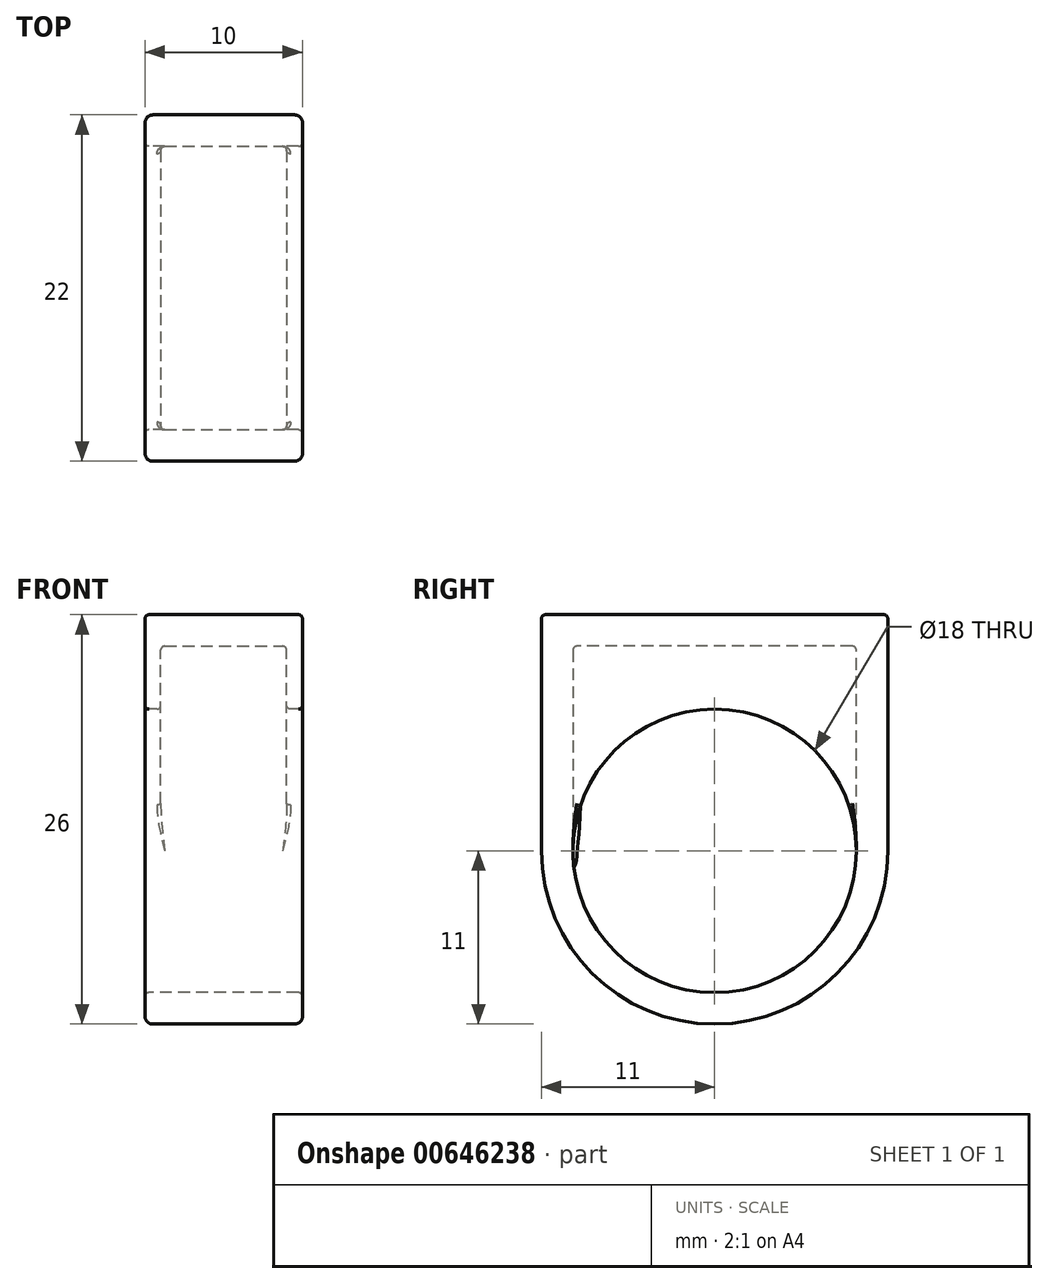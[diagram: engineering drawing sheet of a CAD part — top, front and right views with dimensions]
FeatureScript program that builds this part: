
annotation { "Feature Type Name" : "Feature", "Feature Type Description" : "" }
export const myFeature = defineFeature(function(context is Context, id is Id, definition is map)
    precondition{}
    {
        {
            var Q0;
            Q0=qCreatedBy(makeId("Right.planeOp"),FACE);
            var sketch = newSketch(context, id + "F0", { "sketchPlane" : qUnion([Q0])});
            skCircle(sketch, "E0", {"center": v(0, 0) * mm, "radius": 9 * mm});
            skArc(sketch, "E1", {"start": v(-11, 0) * mm, "mid": v(0, -11) * mm, "end": v(11, 0) * mm});
            skLineSegment(sketch, "E2", {"start": v(11, 0) * mm, "end": v(11, 15) * mm});
            skLineSegment(sketch, "E3", {"start": v(11, 15) * mm, "end": v(-11, 15) * mm});
            skLineSegment(sketch, "E4", {"start": v(-11, 0) * mm, "end": v(-11, 15) * mm});
            skSolve(sketch);
        }
        {
            var Q0;
            Q0 = qSketchRegion(id + "F0", true);
            extrude(context, id + "F1", {"entities" : qUnion([Q0]), "endBound" : BoundingType.SYMMETRIC, "depth" : 10 * mm, "offsetDistance" : 25 * mm});
        }
        {
            var Q0;
            Q0=qCreatedBy(makeId("Right.planeOp"),FACE);
            var sketch = newSketch(context, id + "F2", { "sketchPlane" : qUnion([Q0])});
            skLineSegment(sketch, "E5.0", {"start": v(-9, 13) * mm, "end": v(-9, 0) * mm});
            skLineSegment(sketch, "E5.1", {"start": v(9, 13) * mm, "end": v(-9, 13) * mm});
            skLineSegment(sketch, "E5.2", {"start": v(9, 0) * mm, "end": v(9, 13) * mm});
            skArc(sketch, "E5.3", {"start": v(-9, 0) * mm, "mid": v(0, -9) * mm, "end": v(9, 0) * mm});
            skSolve(sketch);
        }
        {
            var Q0;
            Q0 = qSketchRegion(id + "F2", true);
            extrude(context, id + "F3", {"entities" : qUnion([Q0]), "operationType" : NewBodyOperationType.REMOVE, "endBound" : BoundingType.SYMMETRIC, "oppositeDirection" : true, "depth" : 8 * mm, "offsetDistance" : 25 * mm});
        }
        {
            var Q0;
            Q0=makeQuery(id+"F1.opExtrude","CAP_EDGE",EDGE,{"disambiguationData":[OSD([sQuery(id+"F0.wireOp",EDGE,"E2")])],"isStart":false});
            var Q1;
            Q1=makeQuery(id+"F1.opExtrude","CAP_EDGE",EDGE,{"disambiguationData":[OSD([sQuery(id+"F0.wireOp",EDGE,"E2")])],"isStart":true});
            fillet(context, id + "F4", {"entities" : qUnion([Q0, Q1]), "radius" : .5 * mm, "tangentPropagation" : true, "allowEdgeOverflow" : false});
        }
        {
            var Q0;
            Q0=makeQuery(id+"F4.opFillet","BLEND_EDGE",EDGE,{"blendedFrom":[makeQuery(id+"F1.opExtrude","CAP_EDGE",EDGE,{"disambiguationData":[OSD([sQuery(id+"F0.wireOp",EDGE,"E2")])],"isStart":true}),makeQuery(id+"F1.opExtrude","SWEPT_FACE",FACE,{"disambiguationData":[OSD([sQuery(id+"F0.wireOp",EDGE,"E3")])]})],"blendedInto":[makeQuery(id+"F1.opExtrude","SWEPT_FACE",FACE,{"disambiguationData":[OSD([sQuery(id+"F0.wireOp",EDGE,"E3")])]})]});
            var Q1;
            Q1=makeQuery(id+"F3.boolean.opBoolean","INTERSECT",EDGE,{"derivedFrom":[makeQuery(id+"F1.opExtrude","SWEPT_FACE",FACE,{"disambiguationData":[OSD([sQuery(id+"F0.wireOp",EDGE,"E0")])]}),makeQuery(id+"F3.opExtrude","CAP_FACE",FACE,{"disambiguationData":[OSD([sQuery(id+"F2.wireOp",EDGE,"E5.0"),sQuery(id+"F2.wireOp",EDGE,"E5.1"),sQuery(id+"F2.wireOp",EDGE,"E5.2"),sQuery(id+"F2.wireOp",EDGE,"E5.3")])],"isStart":false})]});
            var Q2;
            Q2=makeQuery(id+"F1.opExtrude","CAP_EDGE",EDGE,{"disambiguationData":[OSD([sQuery(id+"F0.wireOp",EDGE,"E0")])],"isStart":true});
            var Q3;
            Q3=makeQuery(id+"F4.opFillet","BLEND_EDGE",EDGE,{"blendedFrom":[makeQuery(id+"F1.opExtrude","CAP_EDGE",EDGE,{"disambiguationData":[OSD([sQuery(id+"F0.wireOp",EDGE,"E1")])],"isStart":true}),makeQuery(id+"F1.opExtrude","CAP_EDGE",EDGE,{"disambiguationData":[OSD([sQuery(id+"F0.wireOp",EDGE,"E2")])],"isStart":true})],"blendedInto":[]});
            var Q4;
            {var subQ0=sQuery(id+"F0.wireOp",EDGE,"E1");Q4=makeQuery(id+"F4.opFillet","BLEND_EDGE",EDGE,{"blendedFrom":[makeQuery(id+"F1.opExtrude","CAP_EDGE",EDGE,{"disambiguationData":[OSD([subQ0])],"isStart":true}),makeQuery(id+"F1.opExtrude","CAP_FACE",FACE,{"disambiguationData":[OSD([sQuery(id+"F0.wireOp",EDGE,"E0"),subQ0,sQuery(id+"F0.wireOp",EDGE,"E2"),sQuery(id+"F0.wireOp",EDGE,"E3"),sQuery(id+"F0.wireOp",EDGE,"E4")])],"isStart":true})],"blendedInto":[makeQuery(id+"F1.opExtrude","CAP_FACE",FACE,{"disambiguationData":[OSD([sQuery(id+"F0.wireOp",EDGE,"E0"),subQ0,sQuery(id+"F0.wireOp",EDGE,"E2"),sQuery(id+"F0.wireOp",EDGE,"E3"),sQuery(id+"F0.wireOp",EDGE,"E4")])],"isStart":true})]});}
            var Q5;
            Q5=makeQuery(id+"F3.boolean.opBoolean","COPY",EDGE,{"derivedFrom":makeQuery(id+"F3.opExtrude","SWEPT_EDGE",EDGE,{"disambiguationData":[OSD([sQuery(id+"F2.wireOp",EDGE,"E5.0"),sQuery(id+"F2.wireOp",EDGE,"E5.3")])]})});
            var Q6;
            {var subQ0=sQuery(id+"F0.wireOp",EDGE,"E1");Q6=makeQuery(id+"F4.opFillet","BLEND_EDGE",EDGE,{"blendedFrom":[makeQuery(id+"F1.opExtrude","CAP_EDGE",EDGE,{"disambiguationData":[OSD([subQ0])],"isStart":true}),makeQuery(id+"F1.opExtrude","SWEPT_FACE",FACE,{"disambiguationData":[OSD([subQ0])]})],"blendedInto":[makeQuery(id+"F1.opExtrude","SWEPT_FACE",FACE,{"disambiguationData":[OSD([subQ0])]})]});}
            var Q7;
            {var subQ0=sQuery(id+"F0.wireOp",EDGE,"E1");Q7=makeQuery(id+"F4.opFillet","BLEND_EDGE",EDGE,{"blendedFrom":[makeQuery(id+"F1.opExtrude","CAP_EDGE",EDGE,{"disambiguationData":[OSD([subQ0])],"isStart":false}),makeQuery(id+"F1.opExtrude","SWEPT_FACE",FACE,{"disambiguationData":[OSD([subQ0])]})],"blendedInto":[makeQuery(id+"F1.opExtrude","SWEPT_FACE",FACE,{"disambiguationData":[OSD([subQ0])]})]});}
            var Q8;
            Q8=makeQuery(id+"F1.opExtrude","CAP_EDGE",EDGE,{"disambiguationData":[OSD([sQuery(id+"F0.wireOp",EDGE,"E3")])],"isStart":true});
            var Q9;
            Q9=makeQuery(id+"F1.opExtrude","CAP_EDGE",EDGE,{"disambiguationData":[OSD([sQuery(id+"F0.wireOp",EDGE,"E3")])],"isStart":false});
            var Q10;
            {var subQ0=sQuery(id+"F0.wireOp",EDGE,"E2");Q10=makeQuery(id+"F4.opFillet","BLEND_EDGE",EDGE,{"blendedFrom":[makeQuery(id+"F1.opExtrude","CAP_EDGE",EDGE,{"disambiguationData":[OSD([subQ0])],"isStart":true}),makeQuery(id+"F1.opExtrude","SWEPT_FACE",FACE,{"disambiguationData":[OSD([subQ0])]})],"blendedInto":[makeQuery(id+"F1.opExtrude","SWEPT_FACE",FACE,{"disambiguationData":[OSD([subQ0])]})]});}
            var Q11;
            {var subQ0=sQuery(id+"F0.wireOp",EDGE,"E2");Q11=makeQuery(id+"F4.opFillet","BLEND_EDGE",EDGE,{"blendedFrom":[makeQuery(id+"F1.opExtrude","CAP_EDGE",EDGE,{"disambiguationData":[OSD([subQ0])],"isStart":false}),makeQuery(id+"F1.opExtrude","CAP_FACE",FACE,{"disambiguationData":[OSD([sQuery(id+"F0.wireOp",EDGE,"E0"),sQuery(id+"F0.wireOp",EDGE,"E1"),subQ0,sQuery(id+"F0.wireOp",EDGE,"E3"),sQuery(id+"F0.wireOp",EDGE,"E4")])],"isStart":false})],"blendedInto":[makeQuery(id+"F1.opExtrude","CAP_FACE",FACE,{"disambiguationData":[OSD([sQuery(id+"F0.wireOp",EDGE,"E0"),sQuery(id+"F0.wireOp",EDGE,"E1"),subQ0,sQuery(id+"F0.wireOp",EDGE,"E3"),sQuery(id+"F0.wireOp",EDGE,"E4")])],"isStart":false})]});}
            var Q12;
            Q12=makeQuery(id+"F1.opExtrude","SWEPT_EDGE",EDGE,{"disambiguationData":[OSD([sQuery(id+"F0.wireOp",EDGE,"E1"),sQuery(id+"F0.wireOp",EDGE,"E4")])]});
            var Q13;
            Q13=makeQuery(id+"F1.opExtrude","SWEPT_EDGE",EDGE,{"disambiguationData":[OSD([sQuery(id+"F0.wireOp",EDGE,"E1"),sQuery(id+"F0.wireOp",EDGE,"E2")])]});
            var Q14;
            Q14=makeQuery(id+"F1.opExtrude","SWEPT_EDGE",EDGE,{"disambiguationData":[OSD([sQuery(id+"F0.wireOp",EDGE,"E2"),sQuery(id+"F0.wireOp",EDGE,"E3")])]});
            var Q15;
            Q15=makeQuery(id+"F1.opExtrude","SWEPT_EDGE",EDGE,{"disambiguationData":[OSD([sQuery(id+"F0.wireOp",EDGE,"E3"),sQuery(id+"F0.wireOp",EDGE,"E4")])]});
            var Q16;
            Q16=makeQuery(id+"F4.opFillet","BLEND_EDGE",EDGE,{"blendedFrom":[makeQuery(id+"F1.opExtrude","CAP_EDGE",EDGE,{"disambiguationData":[OSD([sQuery(id+"F0.wireOp",EDGE,"E1")])],"isStart":true}),makeQuery(id+"F1.opExtrude","CAP_EDGE",EDGE,{"disambiguationData":[OSD([sQuery(id+"F0.wireOp",EDGE,"E4")])],"isStart":true})],"blendedInto":[]});
            var Q17;
            Q17=makeQuery(id+"F3.boolean.opBoolean","COPY",EDGE,{"derivedFrom":makeQuery(id+"F3.opExtrude","SWEPT_EDGE",EDGE,{"disambiguationData":[OSD([sQuery(id+"F2.wireOp",EDGE,"E5.2"),sQuery(id+"F2.wireOp",EDGE,"E5.3")])]})});
            var Q18;
            Q18=makeQuery(id+"F3.boolean.opBoolean","COPY",EDGE,{"derivedFrom":makeQuery(id+"F3.opExtrude","CAP_EDGE",EDGE,{"disambiguationData":[OSD([sQuery(id+"F2.wireOp",EDGE,"E5.0")])],"isStart":false})});
            var Q19;
            Q19=makeQuery(id+"F1.opExtrude","CAP_EDGE",EDGE,{"disambiguationData":[OSD([sQuery(id+"F0.wireOp",EDGE,"E0")])],"isStart":false});
            var Q20;
            Q20=makeQuery(id+"F3.boolean.opBoolean","COPY",EDGE,{"derivedFrom":makeQuery(id+"F3.opExtrude","SWEPT_EDGE",EDGE,{"disambiguationData":[OSD([sQuery(id+"F2.wireOp",EDGE,"E5.1"),sQuery(id+"F2.wireOp",EDGE,"E5.2")])]})});
            var Q21;
            Q21=makeQuery(id+"F3.boolean.opBoolean","COPY",EDGE,{"derivedFrom":makeQuery(id+"F3.opExtrude","CAP_EDGE",EDGE,{"disambiguationData":[OSD([sQuery(id+"F2.wireOp",EDGE,"E5.1")])],"isStart":true})});
            var Q22;
            Q22=makeQuery(id+"F3.boolean.opBoolean","COPY",EDGE,{"derivedFrom":makeQuery(id+"F3.opExtrude","CAP_EDGE",EDGE,{"disambiguationData":[OSD([sQuery(id+"F2.wireOp",EDGE,"E5.1")])],"isStart":false})});
            var Q23;
            Q23=makeQuery(id+"F3.boolean.opBoolean","COPY",EDGE,{"derivedFrom":makeQuery(id+"F3.opExtrude","SWEPT_EDGE",EDGE,{"disambiguationData":[OSD([sQuery(id+"F2.wireOp",EDGE,"E5.0"),sQuery(id+"F2.wireOp",EDGE,"E5.1")])]})});
            var Q24;
            Q24=makeQuery(id+"F4.opFillet","BLEND_EDGE",EDGE,{"blendedFrom":[makeQuery(id+"F1.opExtrude","CAP_EDGE",EDGE,{"disambiguationData":[OSD([sQuery(id+"F0.wireOp",EDGE,"E1")])],"isStart":false}),makeQuery(id+"F1.opExtrude","CAP_EDGE",EDGE,{"disambiguationData":[OSD([sQuery(id+"F0.wireOp",EDGE,"E2")])],"isStart":false})],"blendedInto":[]});
            var Q25;
            {var subQ0=sQuery(id+"F0.wireOp",EDGE,"E1");Q25=makeQuery(id+"F4.opFillet","BLEND_EDGE",EDGE,{"blendedFrom":[makeQuery(id+"F1.opExtrude","CAP_EDGE",EDGE,{"disambiguationData":[OSD([subQ0])],"isStart":false}),makeQuery(id+"F1.opExtrude","CAP_FACE",FACE,{"disambiguationData":[OSD([sQuery(id+"F0.wireOp",EDGE,"E0"),subQ0,sQuery(id+"F0.wireOp",EDGE,"E2"),sQuery(id+"F0.wireOp",EDGE,"E3"),sQuery(id+"F0.wireOp",EDGE,"E4")])],"isStart":false})],"blendedInto":[makeQuery(id+"F1.opExtrude","CAP_FACE",FACE,{"disambiguationData":[OSD([sQuery(id+"F0.wireOp",EDGE,"E0"),subQ0,sQuery(id+"F0.wireOp",EDGE,"E2"),sQuery(id+"F0.wireOp",EDGE,"E3"),sQuery(id+"F0.wireOp",EDGE,"E4")])],"isStart":false})]});}
            var Q26;
            {var subQ0=sQuery(id+"F0.wireOp",EDGE,"E2");Q26=makeQuery(id+"F4.opFillet","BLEND_EDGE",EDGE,{"blendedFrom":[makeQuery(id+"F1.opExtrude","CAP_EDGE",EDGE,{"disambiguationData":[OSD([subQ0])],"isStart":true}),makeQuery(id+"F1.opExtrude","CAP_FACE",FACE,{"disambiguationData":[OSD([sQuery(id+"F0.wireOp",EDGE,"E0"),sQuery(id+"F0.wireOp",EDGE,"E1"),subQ0,sQuery(id+"F0.wireOp",EDGE,"E3"),sQuery(id+"F0.wireOp",EDGE,"E4")])],"isStart":true})],"blendedInto":[makeQuery(id+"F1.opExtrude","CAP_FACE",FACE,{"disambiguationData":[OSD([sQuery(id+"F0.wireOp",EDGE,"E0"),sQuery(id+"F0.wireOp",EDGE,"E1"),subQ0,sQuery(id+"F0.wireOp",EDGE,"E3"),sQuery(id+"F0.wireOp",EDGE,"E4")])],"isStart":true})]});}
            var Q27;
            {var subQ0=sQuery(id+"F0.wireOp",EDGE,"E2");Q27=makeQuery(id+"F4.opFillet","BLEND_EDGE",EDGE,{"blendedFrom":[makeQuery(id+"F1.opExtrude","CAP_EDGE",EDGE,{"disambiguationData":[OSD([subQ0])],"isStart":false}),makeQuery(id+"F1.opExtrude","SWEPT_FACE",FACE,{"disambiguationData":[OSD([subQ0])]})],"blendedInto":[makeQuery(id+"F1.opExtrude","SWEPT_FACE",FACE,{"disambiguationData":[OSD([subQ0])]})]});}
            var Q28;
            Q28=makeQuery(id+"F4.opFillet","BLEND_EDGE",EDGE,{"blendedFrom":[makeQuery(id+"F1.opExtrude","CAP_EDGE",EDGE,{"disambiguationData":[OSD([sQuery(id+"F0.wireOp",EDGE,"E2")])],"isStart":false}),makeQuery(id+"F1.opExtrude","SWEPT_FACE",FACE,{"disambiguationData":[OSD([sQuery(id+"F0.wireOp",EDGE,"E3")])]})],"blendedInto":[makeQuery(id+"F1.opExtrude","SWEPT_FACE",FACE,{"disambiguationData":[OSD([sQuery(id+"F0.wireOp",EDGE,"E3")])]})]});
            var Q29;
            {var subQ0=sQuery(id+"F0.wireOp",EDGE,"E4");Q29=makeQuery(id+"F4.opFillet","BLEND_EDGE",EDGE,{"blendedFrom":[makeQuery(id+"F1.opExtrude","CAP_EDGE",EDGE,{"disambiguationData":[OSD([subQ0])],"isStart":true}),makeQuery(id+"F1.opExtrude","CAP_FACE",FACE,{"disambiguationData":[OSD([sQuery(id+"F0.wireOp",EDGE,"E0"),sQuery(id+"F0.wireOp",EDGE,"E1"),sQuery(id+"F0.wireOp",EDGE,"E2"),sQuery(id+"F0.wireOp",EDGE,"E3"),subQ0])],"isStart":true})],"blendedInto":[makeQuery(id+"F1.opExtrude","CAP_FACE",FACE,{"disambiguationData":[OSD([sQuery(id+"F0.wireOp",EDGE,"E0"),sQuery(id+"F0.wireOp",EDGE,"E1"),sQuery(id+"F0.wireOp",EDGE,"E2"),sQuery(id+"F0.wireOp",EDGE,"E3"),subQ0])],"isStart":true})]});}
            var Q30;
            Q30=makeQuery(id+"F4.opFillet","BLEND_EDGE",EDGE,{"blendedFrom":[makeQuery(id+"F1.opExtrude","CAP_EDGE",EDGE,{"disambiguationData":[OSD([sQuery(id+"F0.wireOp",EDGE,"E4")])],"isStart":true}),makeQuery(id+"F1.opExtrude","SWEPT_FACE",FACE,{"disambiguationData":[OSD([sQuery(id+"F0.wireOp",EDGE,"E3")])]})],"blendedInto":[makeQuery(id+"F1.opExtrude","SWEPT_FACE",FACE,{"disambiguationData":[OSD([sQuery(id+"F0.wireOp",EDGE,"E3")])]})]});
            var Q31;
            {var subQ0=sQuery(id+"F0.wireOp",EDGE,"E4");Q31=makeQuery(id+"F4.opFillet","BLEND_EDGE",EDGE,{"blendedFrom":[makeQuery(id+"F1.opExtrude","CAP_EDGE",EDGE,{"disambiguationData":[OSD([subQ0])],"isStart":true}),makeQuery(id+"F1.opExtrude","SWEPT_FACE",FACE,{"disambiguationData":[OSD([subQ0])]})],"blendedInto":[makeQuery(id+"F1.opExtrude","SWEPT_FACE",FACE,{"disambiguationData":[OSD([subQ0])]})]});}
            var Q32;
            Q32=makeQuery(id+"F4.opFillet","BLEND_EDGE",EDGE,{"blendedFrom":[makeQuery(id+"F1.opExtrude","CAP_EDGE",EDGE,{"disambiguationData":[OSD([sQuery(id+"F0.wireOp",EDGE,"E4")])],"isStart":false}),makeQuery(id+"F1.opExtrude","SWEPT_FACE",FACE,{"disambiguationData":[OSD([sQuery(id+"F0.wireOp",EDGE,"E3")])]})],"blendedInto":[makeQuery(id+"F1.opExtrude","SWEPT_FACE",FACE,{"disambiguationData":[OSD([sQuery(id+"F0.wireOp",EDGE,"E3")])]})]});
            var Q33;
            Q33=makeQuery(id+"F3.boolean.opBoolean","COPY",EDGE,{"derivedFrom":makeQuery(id+"F3.opExtrude","CAP_EDGE",EDGE,{"disambiguationData":[OSD([sQuery(id+"F2.wireOp",EDGE,"E5.2")])],"isStart":false})});
            var Q34;
            Q34=makeQuery(id+"F3.boolean.opBoolean","INTERSECT",EDGE,{"derivedFrom":[makeQuery(id+"F1.opExtrude","SWEPT_FACE",FACE,{"disambiguationData":[OSD([sQuery(id+"F0.wireOp",EDGE,"E0")])]}),makeQuery(id+"F3.opExtrude","CAP_FACE",FACE,{"disambiguationData":[OSD([sQuery(id+"F2.wireOp",EDGE,"E5.0"),sQuery(id+"F2.wireOp",EDGE,"E5.1"),sQuery(id+"F2.wireOp",EDGE,"E5.2"),sQuery(id+"F2.wireOp",EDGE,"E5.3")])],"isStart":true})]});
            var Q35;
            Q35=makeQuery(id+"F3.boolean.opBoolean","COPY",EDGE,{"derivedFrom":makeQuery(id+"F3.opExtrude","CAP_EDGE",EDGE,{"disambiguationData":[OSD([sQuery(id+"F2.wireOp",EDGE,"E5.0")])],"isStart":true})});
            var Q36;
            Q36=makeQuery(id+"F3.boolean.opBoolean","COPY",EDGE,{"derivedFrom":makeQuery(id+"F3.opExtrude","CAP_EDGE",EDGE,{"disambiguationData":[OSD([sQuery(id+"F2.wireOp",EDGE,"E5.2")])],"isStart":true})});
            var Q37;
            {var subQ0=sQuery(id+"F0.wireOp",EDGE,"E4");Q37=makeQuery(id+"F4.opFillet","BLEND_EDGE",EDGE,{"blendedFrom":[makeQuery(id+"F1.opExtrude","CAP_EDGE",EDGE,{"disambiguationData":[OSD([subQ0])],"isStart":false}),makeQuery(id+"F1.opExtrude","CAP_FACE",FACE,{"disambiguationData":[OSD([sQuery(id+"F0.wireOp",EDGE,"E0"),sQuery(id+"F0.wireOp",EDGE,"E1"),sQuery(id+"F0.wireOp",EDGE,"E2"),sQuery(id+"F0.wireOp",EDGE,"E3"),subQ0])],"isStart":false})],"blendedInto":[makeQuery(id+"F1.opExtrude","CAP_FACE",FACE,{"disambiguationData":[OSD([sQuery(id+"F0.wireOp",EDGE,"E0"),sQuery(id+"F0.wireOp",EDGE,"E1"),sQuery(id+"F0.wireOp",EDGE,"E2"),sQuery(id+"F0.wireOp",EDGE,"E3"),subQ0])],"isStart":false})]});}
            var Q38;
            {var subQ0=sQuery(id+"F0.wireOp",EDGE,"E4");Q38=makeQuery(id+"F4.opFillet","BLEND_EDGE",EDGE,{"blendedFrom":[makeQuery(id+"F1.opExtrude","CAP_EDGE",EDGE,{"disambiguationData":[OSD([subQ0])],"isStart":false}),makeQuery(id+"F1.opExtrude","SWEPT_FACE",FACE,{"disambiguationData":[OSD([subQ0])]})],"blendedInto":[makeQuery(id+"F1.opExtrude","SWEPT_FACE",FACE,{"disambiguationData":[OSD([subQ0])]})]});}
            var Q39;
            Q39=makeQuery(id+"F4.opFillet","BLEND_EDGE",EDGE,{"blendedFrom":[makeQuery(id+"F1.opExtrude","CAP_EDGE",EDGE,{"disambiguationData":[OSD([sQuery(id+"F0.wireOp",EDGE,"E1")])],"isStart":false}),makeQuery(id+"F1.opExtrude","CAP_EDGE",EDGE,{"disambiguationData":[OSD([sQuery(id+"F0.wireOp",EDGE,"E4")])],"isStart":false})],"blendedInto":[]});
            fillet(context, id + "F5", {"entities" : qUnion([Q0, Q1, Q2, Q3, Q4, Q5, Q6, Q7, Q8, Q9, Q10, Q11, Q12, Q13, Q14, Q15, Q16, Q17, Q18, Q19, Q20, Q21, Q22, Q23, Q24, Q25, Q26, Q27, Q28, Q29, Q30, Q31, Q32, Q33, Q34, Q35, Q36, Q37, Q38, Q39]), "radius" : .25 * mm, "tangentPropagation" : true, "allowEdgeOverflow" : false});
        }
    });
